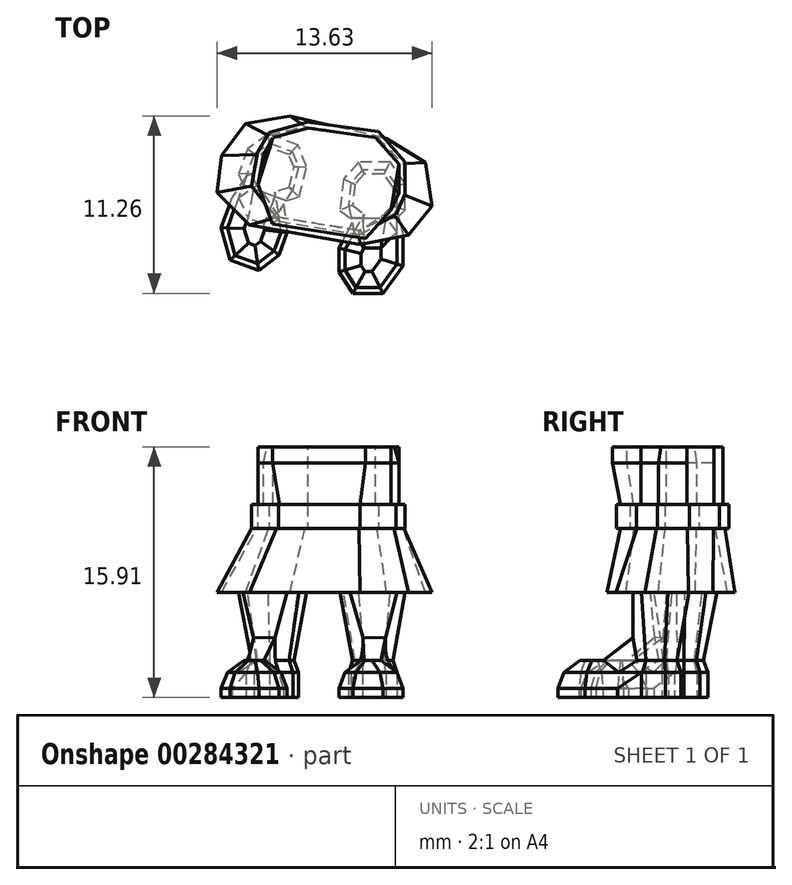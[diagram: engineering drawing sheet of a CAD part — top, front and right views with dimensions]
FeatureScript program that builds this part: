
annotation { "Feature Type Name" : "Feature", "Feature Type Description" : "" }
export const myFeature = defineFeature(function(context is Context, id is Id, definition is map)
    precondition{}
    {
        {
            var Q0;
            Q0=qCreatedBy(makeId("Top.planeOp"),FACE);
            var sketch = newSketch(context, id + "F0", { "sketchPlane" : qUnion([Q0])});
            skLineSegment(sketch, "E0.bottom", {"start": v(0, 0) * mm, "end": v(25.4, 0) * mm});
            skLineSegment(sketch, "E0.top", {"start": v(0, -25.4) * mm, "end": v(25.4, -25.4) * mm});
            skLineSegment(sketch, "E0.left", {"start": v(0, 0) * mm, "end": v(0, -25.4) * mm});
            skLineSegment(sketch, "E0.right", {"start": v(25.4, 0) * mm, "end": v(25.4, -25.4) * mm});
            skLineSegment(sketch, "E1", {"start": v(15.15, -16.75) * mm, "end": v(16.02, -18.11) * mm});
            skLineSegment(sketch, "E2", {"start": v(16.02, -18.11) * mm, "end": v(17.95, -18.11) * mm});
            skLineSegment(sketch, "E3", {"start": v(17.95, -18.11) * mm, "end": v(19.2, -16.37) * mm});
            skLineSegment(sketch, "E4", {"start": v(19.2, -16.37) * mm, "end": v(19.2, -14.33) * mm});
            skLineSegment(sketch, "E5", {"start": v(19.2, -14.33) * mm, "end": v(18.82, -12.78) * mm});
            skLineSegment(sketch, "E6", {"start": v(18.82, -12.78) * mm, "end": v(18.82, -11.27) * mm});
            skLineSegment(sketch, "E7", {"start": v(18.82, -11.27) * mm, "end": v(18.14, -10.28) * mm});
            skLineSegment(sketch, "E8", {"start": v(18.14, -10.28) * mm, "end": v(16.64, -10.28) * mm});
            skLineSegment(sketch, "E9", {"start": v(16.64, -10.28) * mm, "end": v(15.9, -11.08) * mm});
            skLineSegment(sketch, "E10", {"start": v(15.9, -11.08) * mm, "end": v(15.76, -12.51) * mm});
            skLineSegment(sketch, "E11", {"start": v(15.76, -12.51) * mm, "end": v(15.98, -13.61) * mm});
            skLineSegment(sketch, "E12", {"start": v(15.98, -13.61) * mm, "end": v(15.15, -15.24) * mm});
            skLineSegment(sketch, "E13", {"start": v(15.15, -15.24) * mm, "end": v(15.15, -16.75) * mm});
            skLineSegment(sketch, "E14.MirrorCS", {"start": v(11.34, -15.67) * mm, "end": v(10.05, -16.65) * mm});
            skLineSegment(sketch, "E15.MirrorCS", {"start": v(12.22, -11.48) * mm, "end": v(11.63, -12.43) * mm});
            skLineSegment(sketch, "E16.MirrorCS", {"start": v(12.15, -9.08) * mm, "end": v(12.56, -10.08) * mm});
            skLineSegment(sketch, "E17.MirrorCS", {"start": v(9.76, -9.26) * mm, "end": v(10.74, -8.57) * mm});
            skLineSegment(sketch, "E18.MirrorCS", {"start": v(8.24, -16) * mm, "end": v(7.66, -13.93) * mm});
            skLineSegment(sketch, "E19.MirrorCS", {"start": v(8.36, -12.01) * mm, "end": v(9.25, -10.68) * mm});
            skLineSegment(sketch, "E20.MirrorCS", {"start": v(10.74, -8.57) * mm, "end": v(12.15, -9.08) * mm});
            skLineSegment(sketch, "E21.MirrorCS", {"start": v(12.56, -10.08) * mm, "end": v(12.22, -11.48) * mm});
            skLineSegment(sketch, "E22.MirrorCS", {"start": v(11.63, -12.43) * mm, "end": v(11.85, -14.25) * mm});
            skLineSegment(sketch, "E23.MirrorCS", {"start": v(9.25, -10.68) * mm, "end": v(9.76, -9.26) * mm});
            skLineSegment(sketch, "E24.MirrorCS", {"start": v(11.85, -14.25) * mm, "end": v(11.34, -15.67) * mm});
            skLineSegment(sketch, "E25.MirrorCS", {"start": v(7.66, -13.93) * mm, "end": v(8.36, -12.01) * mm});
            skLineSegment(sketch, "E26.MirrorCS", {"start": v(10.05, -16.65) * mm, "end": v(8.24, -16) * mm});
            skSolve(sketch);
        }
        {
            var Q0;
            Q0=makeQuery(id+"F0.imprint","IMPRINT",FACE,{"disambiguationData":[TD([[makeQuery(id+"F0.imprint","IMPRINT",EDGE,{"derivedFrom":sQuery(id+"F0.wireOp",EDGE,"E0.bottom")}),-1.0]])]});
            cPlane(context, id + "F1", {"entities" : qUnion([Q0]), "cplaneType" : CPlaneType.OFFSET, "offset" : 1.59 * mm, "width" : 152.4 * mm, "height" : 152.4 * mm});
        }
        {
            var Q0;
            Q0=makeQuery(id+"F0.imprint","IMPRINT",FACE,{"disambiguationData":[TD([[makeQuery(id+"F0.imprint","IMPRINT",EDGE,{"derivedFrom":sQuery(id+"F0.wireOp",EDGE,"E14.MirrorCS")}),-1.0]])]});
            var Q1;
            Q1=makeQuery(id+"F0.imprint","IMPRINT",FACE,{"disambiguationData":[TD([[makeQuery(id+"F0.imprint","IMPRINT",EDGE,{"derivedFrom":sQuery(id+"F0.wireOp",EDGE,"E1")}),1.0]])]});
            extrude(context, id + "F2", {"entities" : qUnion([Q0, Q1]), "depth" : 1.59 * mm});
        }
        {
            var Q0;
            Q0=makeQuery(id+"F2.opExtrude","CAP_EDGE",EDGE,{"disambiguationData":[OSD([sQuery(id+"F0.wireOp",EDGE,"E4")])],"isStart":false});
            var Q1;
            Q1=makeQuery(id+"F2.opExtrude","CAP_EDGE",EDGE,{"disambiguationData":[OSD([sQuery(id+"F0.wireOp",EDGE,"E3")])],"isStart":false});
            var Q2;
            Q2=makeQuery(id+"F2.opExtrude","CAP_EDGE",EDGE,{"disambiguationData":[OSD([sQuery(id+"F0.wireOp",EDGE,"E2")])],"isStart":false});
            var Q3;
            Q3=makeQuery(id+"F2.opExtrude","CAP_EDGE",EDGE,{"disambiguationData":[OSD([sQuery(id+"F0.wireOp",EDGE,"E1")])],"isStart":false});
            var Q4;
            Q4=makeQuery(id+"F2.opExtrude","CAP_EDGE",EDGE,{"disambiguationData":[OSD([sQuery(id+"F0.wireOp",EDGE,"E13")])],"isStart":false});
            var Q5;
            Q5=makeQuery(id+"F2.opExtrude","CAP_EDGE",EDGE,{"disambiguationData":[OSD([sQuery(id+"F0.wireOp",EDGE,"E12")])],"isStart":false});
            chamfer(context, id + "F3", {"entities" : qUnion([Q0, Q1, Q2, Q3, Q4, Q5]), "chamferType" : ChamferType.TWO_OFFSETS, "width1" : 0.38 * mm, "oppositeDirection" : false, "width2" : 1.02 * mm, "tangentPropagation" : true});
        }
        {
            var Q0;
            Q0=makeQuery(id+"F2.opExtrude","CAP_EDGE",EDGE,{"disambiguationData":[OSD([sQuery(id+"F0.wireOp",EDGE,"E25.MirrorCS")])],"isStart":false});
            var Q1;
            Q1=makeQuery(id+"F2.opExtrude","CAP_EDGE",EDGE,{"disambiguationData":[OSD([sQuery(id+"F0.wireOp",EDGE,"E18.MirrorCS")])],"isStart":false});
            var Q2;
            Q2=makeQuery(id+"F2.opExtrude","CAP_EDGE",EDGE,{"disambiguationData":[OSD([sQuery(id+"F0.wireOp",EDGE,"E26.MirrorCS")])],"isStart":false});
            var Q3;
            Q3=makeQuery(id+"F2.opExtrude","CAP_EDGE",EDGE,{"disambiguationData":[OSD([sQuery(id+"F0.wireOp",EDGE,"E14.MirrorCS")])],"isStart":false});
            var Q4;
            Q4=makeQuery(id+"F2.opExtrude","CAP_EDGE",EDGE,{"disambiguationData":[OSD([sQuery(id+"F0.wireOp",EDGE,"E24.MirrorCS")])],"isStart":false});
            var Q5;
            Q5=makeQuery(id+"F2.opExtrude","CAP_EDGE",EDGE,{"disambiguationData":[OSD([sQuery(id+"F0.wireOp",EDGE,"E22.MirrorCS")])],"isStart":false});
            chamfer(context, id + "F4", {"entities" : qUnion([Q0, Q1, Q2, Q3, Q4, Q5]), "chamferType" : ChamferType.TWO_OFFSETS, "width1" : 1.02 * mm, "oppositeDirection" : false, "width2" : 0.38 * mm, "tangentPropagation" : true});
        }
        {
            var Q0;
            Q0=qCreatedBy(id+"F1.planeOp",FACE);
            var sketch = newSketch(context, id + "F5", { "sketchPlane" : qUnion([Q0])});
            skLineSegment(sketch, "E27.0.0", {"start": v(11.46, -14.2) * mm, "end": v(11.3, -12.95) * mm});
            skLineSegment(sketch, "E27.0.1", {"start": v(11.3, -12.95) * mm, "end": v(12.22, -11.48) * mm});
            skLineSegment(sketch, "E27.0.2", {"start": v(12.22, -11.48) * mm, "end": v(12.56, -10.08) * mm});
            skLineSegment(sketch, "E27.0.3", {"start": v(12.56, -10.08) * mm, "end": v(12.15, -9.08) * mm});
            skLineSegment(sketch, "E27.0.4", {"start": v(12.15, -9.08) * mm, "end": v(10.74, -8.57) * mm});
            skLineSegment(sketch, "E27.0.5", {"start": v(10.74, -8.57) * mm, "end": v(9.77, -9.26) * mm});
            skLineSegment(sketch, "E27.0.6", {"start": v(9.77, -9.26) * mm, "end": v(8.06, -13.94) * mm});
            skLineSegment(sketch, "E27.0.7", {"start": v(8.06, -13.94) * mm, "end": v(8.55, -15.7) * mm});
            skLineSegment(sketch, "E27.0.8", {"start": v(8.55, -15.7) * mm, "end": v(9.99, -16.22) * mm});
            skLineSegment(sketch, "E27.0.9", {"start": v(9.99, -16.22) * mm, "end": v(11.02, -15.43) * mm});
            skLineSegment(sketch, "E27.0.10", {"start": v(11.02, -15.43) * mm, "end": v(11.46, -14.2) * mm});
            skLineSegment(sketch, "E28.0.0", {"start": v(15.76, -12.51) * mm, "end": v(16.1, -14.2) * mm});
            skLineSegment(sketch, "E28.0.1", {"start": v(16.1, -14.2) * mm, "end": v(15.53, -15.33) * mm});
            skLineSegment(sketch, "E28.0.2", {"start": v(15.53, -15.33) * mm, "end": v(15.53, -16.64) * mm});
            skLineSegment(sketch, "E28.0.3", {"start": v(15.53, -16.64) * mm, "end": v(16.23, -17.73) * mm});
            skLineSegment(sketch, "E28.0.4", {"start": v(16.23, -17.73) * mm, "end": v(17.76, -17.73) * mm});
            skLineSegment(sketch, "E28.0.5", {"start": v(17.76, -17.73) * mm, "end": v(18.82, -16.25) * mm});
            skLineSegment(sketch, "E28.0.6", {"start": v(18.82, -16.25) * mm, "end": v(18.82, -11.26) * mm});
            skLineSegment(sketch, "E28.0.7", {"start": v(18.82, -11.26) * mm, "end": v(18.14, -10.28) * mm});
            skLineSegment(sketch, "E28.0.8", {"start": v(18.14, -10.28) * mm, "end": v(16.64, -10.28) * mm});
            skLineSegment(sketch, "E28.0.9", {"start": v(16.64, -10.28) * mm, "end": v(15.9, -11.08) * mm});
            skLineSegment(sketch, "E28.0.10", {"start": v(15.9, -11.08) * mm, "end": v(15.76, -12.51) * mm});
            skLineSegment(sketch, "E29", {"start": v(16.1, -14.2) * mm, "end": v(18.82, -14.2) * mm});
            skLineSegment(sketch, "E30", {"start": v(11.3, -12.95) * mm, "end": v(8.76, -12.03) * mm});
            skSolve(sketch);
        }
        {
            var Q0;
            Q0=qCreatedBy(id+"F1.planeOp",FACE);
            cPlane(context, id + "F6", {"entities" : qUnion([Q0]), "cplaneType" : CPlaneType.OFFSET, "offset" : 0.76 * mm, "width" : 152.4 * mm, "height" : 152.4 * mm});
        }
        {
            var Q0;
            Q0=qCreatedBy(id+"F6.planeOp",FACE);
            var sketch = newSketch(context, id + "F7", { "sketchPlane" : qUnion([Q0])});
            skLineSegment(sketch, "E31.0.0", {"start": v(8.76, -12.03) * mm, "end": v(11.3, -12.95) * mm, "construction": true});
            skLineSegment(sketch, "E31.0.1", {"start": v(11.3, -12.95) * mm, "end": v(12.22, -11.48) * mm, "construction": true});
            skLineSegment(sketch, "E31.0.2", {"start": v(12.22, -11.48) * mm, "end": v(12.56, -10.08) * mm, "construction": true});
            skLineSegment(sketch, "E31.0.3", {"start": v(12.56, -10.08) * mm, "end": v(12.15, -9.08) * mm, "construction": true});
            skLineSegment(sketch, "E31.0.4", {"start": v(12.15, -9.08) * mm, "end": v(10.74, -8.57) * mm, "construction": true});
            skLineSegment(sketch, "E31.0.5", {"start": v(10.74, -8.57) * mm, "end": v(9.77, -9.26) * mm, "construction": true});
            skLineSegment(sketch, "E31.0.6", {"start": v(9.77, -9.26) * mm, "end": v(8.76, -12.03) * mm, "construction": true});
            skLineSegment(sketch, "E32.0.0", {"start": v(11.3, -12.95) * mm, "end": v(8.76, -12.03) * mm, "construction": true});
            skLineSegment(sketch, "E32.0.1", {"start": v(8.76, -12.03) * mm, "end": v(8.06, -13.94) * mm, "construction": true});
            skLineSegment(sketch, "E32.0.2", {"start": v(8.06, -13.94) * mm, "end": v(8.55, -15.7) * mm, "construction": true});
            skLineSegment(sketch, "E32.0.3", {"start": v(8.55, -15.7) * mm, "end": v(9.99, -16.22) * mm, "construction": true});
            skLineSegment(sketch, "E32.0.4", {"start": v(9.99, -16.22) * mm, "end": v(11.02, -15.43) * mm, "construction": true});
            skLineSegment(sketch, "E32.0.5", {"start": v(11.02, -15.43) * mm, "end": v(11.46, -14.2) * mm, "construction": true});
            skLineSegment(sketch, "E32.0.6", {"start": v(11.46, -14.2) * mm, "end": v(11.3, -12.95) * mm, "construction": true});
            skLineSegment(sketch, "E33.0.0", {"start": v(16.1, -14.2) * mm, "end": v(18.82, -14.2) * mm, "construction": true});
            skLineSegment(sketch, "E33.0.1", {"start": v(18.82, -14.2) * mm, "end": v(18.82, -11.26) * mm, "construction": true});
            skLineSegment(sketch, "E33.0.2", {"start": v(18.82, -11.26) * mm, "end": v(18.14, -10.28) * mm, "construction": true});
            skLineSegment(sketch, "E33.0.3", {"start": v(18.14, -10.28) * mm, "end": v(16.64, -10.28) * mm, "construction": true});
            skLineSegment(sketch, "E33.0.4", {"start": v(16.64, -10.28) * mm, "end": v(15.9, -11.08) * mm, "construction": true});
            skLineSegment(sketch, "E33.0.5", {"start": v(15.9, -11.08) * mm, "end": v(15.76, -12.51) * mm, "construction": true});
            skLineSegment(sketch, "E33.0.6", {"start": v(15.76, -12.51) * mm, "end": v(16.1, -14.2) * mm, "construction": true});
            skLineSegment(sketch, "E34.0.0", {"start": v(18.82, -14.2) * mm, "end": v(16.1, -14.2) * mm, "construction": true});
            skLineSegment(sketch, "E34.0.1", {"start": v(16.1, -14.2) * mm, "end": v(15.53, -15.33) * mm, "construction": true});
            skLineSegment(sketch, "E34.0.2", {"start": v(15.53, -15.33) * mm, "end": v(15.53, -16.64) * mm, "construction": true});
            skLineSegment(sketch, "E34.0.3", {"start": v(15.53, -16.64) * mm, "end": v(16.23, -17.73) * mm, "construction": true});
            skLineSegment(sketch, "E34.0.4", {"start": v(16.23, -17.73) * mm, "end": v(17.76, -17.73) * mm, "construction": true});
            skLineSegment(sketch, "E34.0.5", {"start": v(17.76, -17.73) * mm, "end": v(18.82, -16.25) * mm, "construction": true});
            skLineSegment(sketch, "E34.0.6", {"start": v(18.82, -16.25) * mm, "end": v(18.82, -14.2) * mm, "construction": true});
            skLineSegment(sketch, "E35.0", {"start": v(10.42, -14.09) * mm, "end": v(10.38, -13.7) * mm});
            skLineSegment(sketch, "E35.1", {"start": v(10.16, -14.8) * mm, "end": v(10.42, -14.09) * mm});
            skLineSegment(sketch, "E35.2", {"start": v(9.37, -13.33) * mm, "end": v(9.13, -13.98) * mm});
            skLineSegment(sketch, "E35.3", {"start": v(9.13, -13.98) * mm, "end": v(9.4, -14.92) * mm});
            skLineSegment(sketch, "E35.4", {"start": v(9.4, -14.92) * mm, "end": v(9.81, -15.07) * mm});
            skLineSegment(sketch, "E35.5", {"start": v(10.38, -13.7) * mm, "end": v(9.37, -13.33) * mm});
            skLineSegment(sketch, "E35.6", {"start": v(9.81, -15.07) * mm, "end": v(10.16, -14.8) * mm});
            skLineSegment(sketch, "E36.0", {"start": v(9.98, -9.42) * mm, "end": v(9.09, -11.87) * mm, "construction": true});
            skLineSegment(sketch, "E36.1", {"start": v(10.78, -8.85) * mm, "end": v(9.98, -9.42) * mm});
            skLineSegment(sketch, "E36.2", {"start": v(11.2, -12.64) * mm, "end": v(11.98, -11.38) * mm, "construction": true});
            skLineSegment(sketch, "E36.3", {"start": v(11.98, -11.38) * mm, "end": v(12.3, -10.1) * mm});
            skLineSegment(sketch, "E36.4", {"start": v(12.3, -10.1) * mm, "end": v(11.96, -9.28) * mm});
            skLineSegment(sketch, "E36.5", {"start": v(9.09, -11.87) * mm, "end": v(11.2, -12.64) * mm, "construction": true});
            skLineSegment(sketch, "E36.6", {"start": v(11.96, -9.28) * mm, "end": v(10.78, -8.85) * mm});
            skLineSegment(sketch, "E37", {"start": v(11.98, -11.38) * mm, "end": v(11.1, -11.67) * mm});
            skLineSegment(sketch, "E38", {"start": v(11.1, -11.67) * mm, "end": v(9.9, -11.24) * mm});
            skLineSegment(sketch, "E39", {"start": v(9.9, -11.24) * mm, "end": v(9.58, -10.5) * mm});
            skLineSegment(sketch, "E40", {"start": v(9.58, -10.5) * mm, "end": v(11.98, -11.38) * mm, "construction": true});
            skLineSegment(sketch, "E41", {"start": v(11.96, -9.28) * mm, "end": v(11.1, -11.67) * mm, "construction": true});
            skLineSegment(sketch, "E42", {"start": v(9.9, -11.24) * mm, "end": v(10.78, -8.85) * mm, "construction": true});
            skLineSegment(sketch, "E43", {"start": v(9.98, -9.42) * mm, "end": v(9.58, -10.5) * mm});
            skLineSegment(sketch, "E44", {"start": v(9.37, -13.33) * mm, "end": v(9.9, -11.24) * mm});
            skLineSegment(sketch, "E45", {"start": v(11.1, -11.67) * mm, "end": v(10.38, -13.7) * mm});
            skLineSegment(sketch, "E46.0", {"start": v(16.73, -15.22) * mm, "end": v(16.55, -15.57) * mm});
            skLineSegment(sketch, "E46.1", {"start": v(16.55, -15.57) * mm, "end": v(16.55, -16.34) * mm});
            skLineSegment(sketch, "E46.2", {"start": v(17.8, -15.92) * mm, "end": v(17.8, -15.22) * mm});
            skLineSegment(sketch, "E46.3", {"start": v(17.23, -16.71) * mm, "end": v(17.8, -15.92) * mm});
            skLineSegment(sketch, "E46.4", {"start": v(16.79, -16.71) * mm, "end": v(17.23, -16.71) * mm});
            skLineSegment(sketch, "E46.5", {"start": v(16.73, -15.22) * mm, "end": v(17.8, -15.22) * mm});
            skLineSegment(sketch, "E46.6", {"start": v(16.55, -16.34) * mm, "end": v(16.79, -16.71) * mm});
            skLineSegment(sketch, "E47.0", {"start": v(16.31, -13.95) * mm, "end": v(18.56, -13.95) * mm, "construction": true});
            skLineSegment(sketch, "E47.1", {"start": v(16.01, -12.5) * mm, "end": v(16.31, -13.95) * mm, "construction": true});
            skLineSegment(sketch, "E47.2", {"start": v(18.56, -11.34) * mm, "end": v(18, -10.54) * mm});
            skLineSegment(sketch, "E47.3", {"start": v(18, -10.54) * mm, "end": v(16.75, -10.54) * mm});
            skLineSegment(sketch, "E47.4", {"start": v(16.75, -10.54) * mm, "end": v(16.15, -11.19) * mm});
            skLineSegment(sketch, "E47.5", {"start": v(18.56, -13.95) * mm, "end": v(18.56, -11.34) * mm, "construction": true});
            skLineSegment(sketch, "E47.6", {"start": v(16.15, -11.19) * mm, "end": v(16.01, -12.5) * mm});
            skLineSegment(sketch, "E48", {"start": v(16.01, -12.5) * mm, "end": v(18.56, -12.5) * mm, "construction": true});
            skLineSegment(sketch, "E49", {"start": v(18.56, -12.5) * mm, "end": v(18, -13.08) * mm});
            skLineSegment(sketch, "E50", {"start": v(18, -13.08) * mm, "end": v(17.8, -15.22) * mm});
            skLineSegment(sketch, "E51", {"start": v(16.01, -12.5) * mm, "end": v(16.75, -13.08) * mm});
            skLineSegment(sketch, "E52", {"start": v(16.75, -13.08) * mm, "end": v(16.73, -15.22) * mm});
            skLineSegment(sketch, "E53", {"start": v(16.75, -10.54) * mm, "end": v(16.75, -13.08) * mm, "construction": true});
            skLineSegment(sketch, "E54", {"start": v(18, -13.08) * mm, "end": v(16.75, -13.08) * mm});
            skLineSegment(sketch, "E55", {"start": v(18, -13.08) * mm, "end": v(18, -10.54) * mm, "construction": true});
            skLineSegment(sketch, "E56", {"start": v(18.56, -11.34) * mm, "end": v(18.56, -12.5) * mm});
            skSolve(sketch);
        }
        {
            var Q1;
            Q1=makeQuery(id+"F5.imprint","IMPRINT",FACE,{"disambiguationData":[TD([[makeQuery(id+"F5.imprint","IMPRINT",EDGE,{"derivedFrom":sQuery(id+"F5.wireOp",EDGE,"E27.0.1")}),1.0]])]});
            var Q2;
            Q2=makeQuery(id+"F7.imprint","IMPRINT",FACE,{"disambiguationData":[TD([[makeQuery(id+"F7.imprint","IMPRINT",EDGE,{"derivedFrom":sQuery(id+"F7.wireOp",EDGE,"E36.1")}),1.0]])]});
            var Q3;
            Q3=sQuery(id+"F5.wireOp",VERTEX,"E27.0.6.start");
            var Q4;
            Q4=sQuery(id+"F7.wireOp",VERTEX,"E36.1.end");
            loft(context, id + "F8", {"operationType" : NewBodyOperationType.ADD, "sheetProfilesArray" : [{ "sheetProfileEntities" : qUnion([Q1]) }, { "sheetProfileEntities" : qUnion([Q2]) }], "matchConnections" : true, "connections" : [{ "connectionEntities" : qUnion([Q3, Q4]), "connectionEdgeQueries" : qUnion([]), "connectionEdgeParameters" : [] }]});
        }
        {
            var Q1;
            Q1=makeQuery(id+"F5.imprint","IMPRINT",FACE,{"disambiguationData":[TD([[makeQuery(id+"F5.imprint","IMPRINT",EDGE,{"derivedFrom":sQuery(id+"F5.wireOp",EDGE,"E28.0.0")}),1.0]])]});
            var Q2;
            Q2=makeQuery(id+"F7.imprint","IMPRINT",FACE,{"disambiguationData":[TD([[makeQuery(id+"F7.imprint","IMPRINT",EDGE,{"derivedFrom":sQuery(id+"F7.wireOp",EDGE,"E47.2")}),1.0]])]});
            var Q3;
            Q3=sQuery(id+"F5.wireOp",VERTEX,"E29.end");
            var Q4;
            Q4=sQuery(id+"F7.wireOp",VERTEX,"E50.start");
            loft(context, id + "F9", {"operationType" : NewBodyOperationType.ADD, "sheetProfilesArray" : [{ "sheetProfileEntities" : qUnion([Q1]) }, { "sheetProfileEntities" : qUnion([Q2]) }], "matchConnections" : true, "connections" : [{ "connectionEntities" : qUnion([Q3, Q4]), "connectionEdgeQueries" : qUnion([]), "connectionEdgeParameters" : [] }]});
        }
        {
            var Q1;
            Q1=makeQuery(id+"F5.imprint","IMPRINT",FACE,{"disambiguationData":[TD([[makeQuery(id+"F5.imprint","IMPRINT",EDGE,{"derivedFrom":sQuery(id+"F5.wireOp",EDGE,"E27.0.0")}),1.0]])]});
            var Q2;
            Q2=makeQuery(id+"F7.imprint","IMPRINT",FACE,{"disambiguationData":[TD([[makeQuery(id+"F7.imprint","IMPRINT",EDGE,{"derivedFrom":sQuery(id+"F7.wireOp",EDGE,"E35.0")}),1.0]])]});
            loft(context, id + "F10", {"operationType" : NewBodyOperationType.ADD, "sheetProfilesArray" : [{ "sheetProfileEntities" : qUnion([Q1]) }, { "sheetProfileEntities" : qUnion([Q2]) }]});
        }
        {
            var Q1;
            Q1=makeQuery(id+"F5.imprint","IMPRINT",FACE,{"disambiguationData":[TD([[makeQuery(id+"F5.imprint","IMPRINT",EDGE,{"derivedFrom":sQuery(id+"F5.wireOp",EDGE,"E28.0.1")}),1.0]])]});
            var Q2;
            Q2=makeQuery(id+"F7.imprint","IMPRINT",FACE,{"disambiguationData":[TD([[makeQuery(id+"F7.imprint","IMPRINT",EDGE,{"derivedFrom":sQuery(id+"F7.wireOp",EDGE,"E46.0")}),1.0]])]});
            loft(context, id + "F11", {"operationType" : NewBodyOperationType.ADD, "sheetProfilesArray" : [{ "sheetProfileEntities" : qUnion([Q1]) }, { "sheetProfileEntities" : qUnion([Q2]) }]});
        }
        {
            var Q0;
            Q0=qCreatedBy(id+"F6.planeOp",FACE);
            cPlane(context, id + "F12", {"entities" : qUnion([Q0]), "cplaneType" : CPlaneType.OFFSET, "offset" : 4.32 * mm, "width" : 152.4 * mm, "height" : 152.4 * mm});
        }
        {
            var Q0;
            Q0=qCreatedBy(id+"F12.planeOp",FACE);
            var sketch = newSketch(context, id + "F13", { "sketchPlane" : qUnion([Q0])});
            skLineSegment(sketch, "E57.0.0", {"start": v(11.1, -11.67) * mm, "end": v(11.98, -11.38) * mm, "construction": true});
            skLineSegment(sketch, "E57.0.1", {"start": v(11.98, -11.38) * mm, "end": v(12.3, -10.1) * mm, "construction": true});
            skLineSegment(sketch, "E57.0.2", {"start": v(12.3, -10.1) * mm, "end": v(11.96, -9.28) * mm, "construction": true});
            skLineSegment(sketch, "E57.0.3", {"start": v(11.96, -9.28) * mm, "end": v(10.78, -8.85) * mm, "construction": true});
            skLineSegment(sketch, "E57.0.4", {"start": v(10.78, -8.85) * mm, "end": v(9.98, -9.42) * mm, "construction": true});
            skLineSegment(sketch, "E57.0.5", {"start": v(9.98, -9.42) * mm, "end": v(9.58, -10.5) * mm, "construction": true});
            skLineSegment(sketch, "E57.0.6", {"start": v(9.58, -10.5) * mm, "end": v(9.9, -11.24) * mm, "construction": true});
            skLineSegment(sketch, "E57.0.7", {"start": v(9.9, -11.24) * mm, "end": v(11.1, -11.67) * mm, "construction": true});
            skLineSegment(sketch, "E58.0.0", {"start": v(18, -13.08) * mm, "end": v(18.56, -12.5) * mm, "construction": true});
            skLineSegment(sketch, "E58.0.1", {"start": v(18.56, -12.5) * mm, "end": v(18.56, -11.34) * mm, "construction": true});
            skLineSegment(sketch, "E58.0.2", {"start": v(18.56, -11.34) * mm, "end": v(18, -10.54) * mm, "construction": true});
            skLineSegment(sketch, "E58.0.3", {"start": v(18, -10.54) * mm, "end": v(16.75, -10.54) * mm, "construction": true});
            skLineSegment(sketch, "E58.0.4", {"start": v(16.75, -10.54) * mm, "end": v(16.15, -11.19) * mm, "construction": true});
            skLineSegment(sketch, "E58.0.5", {"start": v(16.15, -11.19) * mm, "end": v(16.01, -12.5) * mm, "construction": true});
            skLineSegment(sketch, "E58.0.6", {"start": v(16.01, -12.5) * mm, "end": v(16.75, -13.08) * mm, "construction": true});
            skLineSegment(sketch, "E58.0.7", {"start": v(16.75, -13.08) * mm, "end": v(18, -13.08) * mm, "construction": true});
            skLineSegment(sketch, "E59.0", {"start": v(19.33, -12.8) * mm, "end": v(19.33, -11.1) * mm});
            skLineSegment(sketch, "E59.1", {"start": v(18.33, -13.84) * mm, "end": v(19.33, -12.8) * mm});
            skLineSegment(sketch, "E59.2", {"start": v(19.33, -11.1) * mm, "end": v(18.4, -9.78) * mm});
            skLineSegment(sketch, "E59.3", {"start": v(16.49, -13.84) * mm, "end": v(18.33, -13.84) * mm});
            skLineSegment(sketch, "E59.4", {"start": v(18.4, -9.78) * mm, "end": v(16.41, -9.78) * mm});
            skLineSegment(sketch, "E59.5", {"start": v(16.41, -9.78) * mm, "end": v(15.42, -10.86) * mm});
            skLineSegment(sketch, "E59.6", {"start": v(15.42, -10.86) * mm, "end": v(15.21, -12.84) * mm});
            skLineSegment(sketch, "E59.7", {"start": v(15.21, -12.84) * mm, "end": v(16.49, -13.84) * mm});
            skLineSegment(sketch, "E60.0", {"start": v(10.66, -8) * mm, "end": v(9.35, -8.94) * mm});
            skLineSegment(sketch, "E60.1", {"start": v(12.54, -8.68) * mm, "end": v(10.66, -8) * mm});
            skLineSegment(sketch, "E60.2", {"start": v(9.35, -8.94) * mm, "end": v(8.76, -10.54) * mm});
            skLineSegment(sketch, "E60.3", {"start": v(13.1, -10.04) * mm, "end": v(12.54, -8.68) * mm});
            skLineSegment(sketch, "E60.4", {"start": v(8.76, -10.54) * mm, "end": v(9.34, -11.85) * mm});
            skLineSegment(sketch, "E60.5", {"start": v(9.34, -11.85) * mm, "end": v(11.08, -12.48) * mm});
            skLineSegment(sketch, "E60.6", {"start": v(11.08, -12.48) * mm, "end": v(12.62, -11.97) * mm});
            skLineSegment(sketch, "E60.7", {"start": v(12.62, -11.97) * mm, "end": v(13.1, -10.04) * mm});
            skSolve(sketch);
        }
        {
            var Q1;
            Q1=makeQuery(id+"F8.opLoft","CAP_FACE",FACE,{"disambiguationData":[OSD([makeQuery(id+"F7.imprint","IMPRINT",FACE,{"disambiguationData":[TD([[makeQuery(id+"F7.imprint","IMPRINT",EDGE,{"derivedFrom":sQuery(id+"F7.wireOp",EDGE,"E36.1")}),1.0]])]})])],"isStart":true});
            var Q2;
            Q2=makeQuery(id+"F13.imprint","IMPRINT",FACE,{"disambiguationData":[TD([[makeQuery(id+"F13.imprint","IMPRINT",EDGE,{"derivedFrom":sQuery(id+"F13.wireOp",EDGE,"E60.0")}),1.0]])]});
            loft(context, id + "F14", {"operationType" : NewBodyOperationType.ADD, "sheetProfilesArray" : [{ "sheetProfileEntities" : qUnion([Q1]) }, { "sheetProfileEntities" : qUnion([Q2]) }]});
        }
        {
            var Q1;
            Q1=makeQuery(id+"F9.opLoft","CAP_FACE",FACE,{"disambiguationData":[OSD([makeQuery(id+"F7.imprint","IMPRINT",FACE,{"disambiguationData":[TD([[makeQuery(id+"F7.imprint","IMPRINT",EDGE,{"derivedFrom":sQuery(id+"F7.wireOp",EDGE,"E47.2")}),1.0]])]})])],"isStart":true});
            var Q2;
            Q2=makeQuery(id+"F13.imprint","IMPRINT",FACE,{"disambiguationData":[TD([[makeQuery(id+"F13.imprint","IMPRINT",EDGE,{"derivedFrom":sQuery(id+"F13.wireOp",EDGE,"E59.0")}),1.0]])]});
            loft(context, id + "F15", {"operationType" : NewBodyOperationType.ADD, "sheetProfilesArray" : [{ "sheetProfileEntities" : qUnion([Q1]) }, { "sheetProfileEntities" : qUnion([Q2]) }]});
        }
        {
            var Q0;
            Q0=makeQuery(id+"F15.opLoft","CAP_FACE",FACE,{"disambiguationData":[OSD([makeQuery(id+"F13.imprint","IMPRINT",FACE,{"disambiguationData":[TD([[makeQuery(id+"F13.imprint","IMPRINT",EDGE,{"derivedFrom":sQuery(id+"F13.wireOp",EDGE,"E59.0")}),1.0]])]})])],"isStart":true});
            var sketch = newSketch(context, id + "F16", { "sketchPlane" : qUnion([Q0])});
            skLineSegment(sketch, "E61.0.0", {"start": v(15.42, -10.86) * mm, "end": v(15.21, -12.84) * mm});
            skLineSegment(sketch, "E61.0.1", {"start": v(15.21, -12.84) * mm, "end": v(16.49, -13.84) * mm});
            skLineSegment(sketch, "E61.0.2", {"start": v(16.49, -13.84) * mm, "end": v(18.33, -13.84) * mm});
            skLineSegment(sketch, "E61.0.3", {"start": v(18.33, -13.84) * mm, "end": v(19.33, -12.8) * mm});
            skLineSegment(sketch, "E61.0.4", {"start": v(19.33, -12.8) * mm, "end": v(19.33, -11.1) * mm});
            skLineSegment(sketch, "E61.0.5", {"start": v(19.33, -11.1) * mm, "end": v(18.4, -9.78) * mm});
            skLineSegment(sketch, "E61.0.6", {"start": v(18.4, -9.78) * mm, "end": v(16.41, -9.78) * mm});
            skLineSegment(sketch, "E61.0.7", {"start": v(16.41, -9.78) * mm, "end": v(15.42, -10.86) * mm});
            skLineSegment(sketch, "E62.0.0", {"start": v(11.08, -12.48) * mm, "end": v(12.62, -11.97) * mm});
            skLineSegment(sketch, "E62.0.1", {"start": v(12.62, -11.97) * mm, "end": v(13.1, -10.04) * mm});
            skLineSegment(sketch, "E62.0.2", {"start": v(13.1, -10.04) * mm, "end": v(12.54, -8.68) * mm});
            skLineSegment(sketch, "E62.0.3", {"start": v(12.54, -8.68) * mm, "end": v(10.66, -8) * mm});
            skLineSegment(sketch, "E62.0.4", {"start": v(10.66, -8) * mm, "end": v(9.35, -8.94) * mm});
            skLineSegment(sketch, "E62.0.5", {"start": v(9.35, -8.94) * mm, "end": v(8.76, -10.54) * mm});
            skLineSegment(sketch, "E62.0.6", {"start": v(8.76, -10.54) * mm, "end": v(9.34, -11.85) * mm});
            skLineSegment(sketch, "E62.0.7", {"start": v(9.34, -11.85) * mm, "end": v(11.08, -12.48) * mm});
            skLineSegment(sketch, "E63", {"start": v(15.85, -13.34) * mm, "end": v(18.83, -13.32) * mm});
            skLineSegment(sketch, "E64", {"start": v(9.05, -11.2) * mm, "end": v(11.85, -12.23) * mm});
            skSolve(sketch);
        }
        {
            var Q0;
            {var subQ0=sQuery(id+"F16.wireOp",EDGE,"E61.0.2");Q0=makeQuery(id+"F16.imprint","IMPRINT",FACE,{"disambiguationData":[TD([[makeQuery(id+"F16.imprint","IMPRINT",EDGE,{"derivedFrom":subQ0}),1.0]])]});}
            var Q1;
            {var subQ0=sQuery(id+"F16.wireOp",EDGE,"E62.0.7");Q1=makeQuery(id+"F16.imprint","IMPRINT",FACE,{"disambiguationData":[TD([[makeQuery(id+"F16.imprint","IMPRINT",EDGE,{"derivedFrom":subQ0}),1.0]])]});}
            extrude(context, id + "F17", {"entities" : qUnion([Q0, Q1]), "operationType" : NewBodyOperationType.REMOVE, "oppositeDirection" : true, "depth" : 3.8 * mm});
        }
        {
            var Q1;
            Q1=makeQuery(id+"F15.opLoft","SWEPT_FACE",FACE,{"disambiguationData":[OSD([sQuery(id+"F7.wireOp",EDGE,"E49"),sQuery(id+"F7.wireOp",EDGE,"E50"),sQuery(id+"F7.wireOp",EDGE,"E51"),sQuery(id+"F7.wireOp",EDGE,"E52"),sQuery(id+"F7.wireOp",EDGE,"E54"),sQuery(id+"F13.wireOp",EDGE,"E59.1"),sQuery(id+"F13.wireOp",EDGE,"E59.3"),sQuery(id+"F13.wireOp",EDGE,"E59.7")])]});
            var Q2;
            Q2=makeQuery(id+"F11.opLoft","SWEPT_FACE",FACE,{"disambiguationData":[OSD([sQuery(id+"F5.wireOp",EDGE,"E28.0.0"),sQuery(id+"F5.wireOp",EDGE,"E28.0.1"),sQuery(id+"F5.wireOp",EDGE,"E28.0.6"),sQuery(id+"F5.wireOp",EDGE,"E29"),sQuery(id+"F7.wireOp",EDGE,"E46.0"),sQuery(id+"F7.wireOp",EDGE,"E46.2"),sQuery(id+"F7.wireOp",EDGE,"E46.5"),sQuery(id+"F7.wireOp",EDGE,"E50"),sQuery(id+"F7.wireOp",EDGE,"E52")])]});
            loft(context, id + "F18", {"operationType" : NewBodyOperationType.ADD, "sheetProfilesArray" : [{ "sheetProfileEntities" : qUnion([Q1]) }, { "sheetProfileEntities" : qUnion([Q2]) }]});
        }
        {
            var Q1;
            Q1=makeQuery(id+"F14.opLoft","SWEPT_FACE",FACE,{"disambiguationData":[OSD([sQuery(id+"F7.wireOp",EDGE,"E37"),sQuery(id+"F7.wireOp",EDGE,"E38"),sQuery(id+"F7.wireOp",EDGE,"E39"),sQuery(id+"F7.wireOp",EDGE,"E44"),sQuery(id+"F7.wireOp",EDGE,"E45"),sQuery(id+"F13.wireOp",EDGE,"E60.4"),sQuery(id+"F13.wireOp",EDGE,"E60.5"),sQuery(id+"F13.wireOp",EDGE,"E60.6")])]});
            var Q2;
            Q2=makeQuery(id+"F10.opLoft","SWEPT_FACE",FACE,{"disambiguationData":[OSD([sQuery(id+"F5.wireOp",EDGE,"E27.0.0"),sQuery(id+"F5.wireOp",EDGE,"E27.0.1"),sQuery(id+"F5.wireOp",EDGE,"E27.0.6"),sQuery(id+"F5.wireOp",EDGE,"E30"),sQuery(id+"F7.wireOp",EDGE,"E35.0"),sQuery(id+"F7.wireOp",EDGE,"E35.2"),sQuery(id+"F7.wireOp",EDGE,"E35.5"),sQuery(id+"F7.wireOp",EDGE,"E44"),sQuery(id+"F7.wireOp",EDGE,"E45")])]});
            loft(context, id + "F19", {"operationType" : NewBodyOperationType.ADD, "sheetProfilesArray" : [{ "sheetProfileEntities" : qUnion([Q1]) }, { "sheetProfileEntities" : qUnion([Q2]) }]});
        }
        {
            var Q0;
            Q0=qCreatedBy(id+"F12.planeOp",FACE);
            var sketch = newSketch(context, id + "F20", { "sketchPlane" : qUnion([Q0])});
            skLineSegment(sketch, "E65", {"start": v(7.68, -9.37) * mm, "end": v(7.4, -11.71) * mm});
            skLineSegment(sketch, "E66", {"start": v(7.4, -11.71) * mm, "end": v(9.47, -13.77) * mm});
            skLineSegment(sketch, "E67", {"start": v(9.47, -13.77) * mm, "end": v(16.47, -15) * mm});
            skLineSegment(sketch, "E68", {"start": v(16.47, -15) * mm, "end": v(19.56, -14.42) * mm});
            skLineSegment(sketch, "E69", {"start": v(19.56, -14.42) * mm, "end": v(21.04, -12.57) * mm});
            skLineSegment(sketch, "E70", {"start": v(21.04, -12.57) * mm, "end": v(20.65, -9.8) * mm});
            skLineSegment(sketch, "E71", {"start": v(20.65, -9.8) * mm, "end": v(18.18, -8.26) * mm});
            skLineSegment(sketch, "E72", {"start": v(18.18, -8.26) * mm, "end": v(12.04, -6.85) * mm});
            skLineSegment(sketch, "E73", {"start": v(12.04, -6.85) * mm, "end": v(9.22, -7.32) * mm});
            skLineSegment(sketch, "E74", {"start": v(9.22, -7.32) * mm, "end": v(7.68, -9.37) * mm});
            skSolve(sketch);
        }
        {
            var Q0;
            Q0=qCreatedBy(id+"F12.planeOp",FACE);
            cPlane(context, id + "F21", {"entities" : qUnion([Q0]), "cplaneType" : CPlaneType.OFFSET, "offset" : 4.83 * mm, "width" : 152.4 * mm, "height" : 152.4 * mm});
        }
        {
            var Q0;
            Q0=qCreatedBy(id+"F21.planeOp",FACE);
            var sketch = newSketch(context, id + "F22", { "sketchPlane" : qUnion([Q0])});
            skLineSegment(sketch, "E75", {"start": v(19.28, 6.58) * mm, "end": v(19.28, -12.05) * mm, "construction": true});
            skLineSegment(sketch, "E76", {"start": v(10.34, 2.97) * mm, "end": v(10.34, -15.66) * mm, "construction": true});
            skLineSegment(sketch, "E77", {"start": v(18.46, -12.83) * mm, "end": v(18.96, -11.7) * mm});
            skLineSegment(sketch, "E78", {"start": v(18.96, -11.7) * mm, "end": v(18.96, -9.9) * mm});
            skLineSegment(sketch, "E79", {"start": v(18.96, -9.9) * mm, "end": v(17.46, -8.2) * mm});
            skLineSegment(sketch, "E80", {"start": v(17.46, -8.2) * mm, "end": v(13.17, -7.62) * mm});
            skLineSegment(sketch, "E81", {"start": v(13.17, -7.62) * mm, "end": v(10.95, -8.22) * mm});
            skLineSegment(sketch, "E82", {"start": v(10.95, -8.22) * mm, "end": v(10.34, -9.28) * mm});
            skLineSegment(sketch, "E83", {"start": v(10.34, -9.28) * mm, "end": v(10, -11.2) * mm});
            skLineSegment(sketch, "E84", {"start": v(10, -11.2) * mm, "end": v(11.52, -13.17) * mm});
            skLineSegment(sketch, "E85", {"start": v(11.52, -13.17) * mm, "end": v(16.4, -13.98) * mm});
            skLineSegment(sketch, "E86", {"start": v(16.4, -13.98) * mm, "end": v(18.46, -12.83) * mm});
            skLineSegment(sketch, "E87.0", {"start": v(19.34, -9.75) * mm, "end": v(17.65, -7.84) * mm});
            skLineSegment(sketch, "E87.1", {"start": v(19.34, -11.78) * mm, "end": v(19.34, -9.75) * mm});
            skLineSegment(sketch, "E87.2", {"start": v(17.65, -7.84) * mm, "end": v(13.14, -7.23) * mm});
            skLineSegment(sketch, "E87.3", {"start": v(18.75, -13.1) * mm, "end": v(19.34, -11.78) * mm});
            skLineSegment(sketch, "E87.4", {"start": v(16.47, -14.37) * mm, "end": v(18.75, -13.1) * mm});
            skLineSegment(sketch, "E87.5", {"start": v(11.3, -13.53) * mm, "end": v(16.47, -14.37) * mm});
            skLineSegment(sketch, "E87.6", {"start": v(13.14, -7.23) * mm, "end": v(10.7, -7.9) * mm});
            skLineSegment(sketch, "E87.7", {"start": v(10.7, -7.9) * mm, "end": v(9.98, -9.15) * mm});
            skLineSegment(sketch, "E87.8", {"start": v(9.98, -9.15) * mm, "end": v(9.6, -11.3) * mm});
            skLineSegment(sketch, "E87.9", {"start": v(9.6, -11.3) * mm, "end": v(11.3, -13.53) * mm});
            skSolve(sketch);
        }
        {
            var Q0;
            Q0=makeQuery(id+"F20.imprint","IMPRINT",FACE,{"disambiguationData":[TD([[makeQuery(id+"F20.imprint","IMPRINT",EDGE,{"derivedFrom":sQuery(id+"F20.wireOp",EDGE,"E65")}),1.0]])]});
            var Q1;
            Q1=makeQuery(id+"F22.imprint","IMPRINT",FACE,{"disambiguationData":[TD([[makeQuery(id+"F22.imprint","IMPRINT",EDGE,{"derivedFrom":sQuery(id+"F22.wireOp",EDGE,"E77")}),1.0]])]});
            loft(context, id + "F23", {"sheetProfilesArray" : [{ "sheetProfileEntities" : qUnion([Q0]) }, { "sheetProfileEntities" : qUnion([Q1]) }]});
        }
        {
            var Q0;
            Q0=qCreatedBy(id+"F21.planeOp",FACE);
            cPlane(context, id + "F24", {"entities" : qUnion([Q0]), "cplaneType" : CPlaneType.OFFSET, "offset" : 3.4 * mm, "width" : 152.4 * mm, "height" : 152.4 * mm});
        }
        {
            var Q0;
            Q0=qCreatedBy(id+"F24.planeOp",FACE);
            var sketch = newSketch(context, id + "F25", { "sketchPlane" : qUnion([Q0])});
            skLineSegment(sketch, "E88.0.0", {"start": v(11.52, -13.17) * mm, "end": v(16.4, -13.98) * mm, "construction": true});
            skLineSegment(sketch, "E88.0.1", {"start": v(16.4, -13.98) * mm, "end": v(18.46, -12.83) * mm, "construction": true});
            skLineSegment(sketch, "E88.0.2", {"start": v(18.46, -12.83) * mm, "end": v(18.96, -11.7) * mm});
            skLineSegment(sketch, "E88.0.3", {"start": v(18.96, -11.7) * mm, "end": v(18.96, -9.9) * mm});
            skLineSegment(sketch, "E88.0.4", {"start": v(18.96, -9.9) * mm, "end": v(17.46, -8.2) * mm});
            skLineSegment(sketch, "E88.0.5", {"start": v(17.46, -8.2) * mm, "end": v(13.17, -7.62) * mm});
            skLineSegment(sketch, "E88.0.6", {"start": v(13.17, -7.62) * mm, "end": v(10.95, -8.22) * mm});
            skLineSegment(sketch, "E88.0.7", {"start": v(10.95, -8.22) * mm, "end": v(10.34, -9.28) * mm});
            skLineSegment(sketch, "E88.0.8", {"start": v(10.34, -9.28) * mm, "end": v(10, -11.2) * mm});
            skLineSegment(sketch, "E88.0.9", {"start": v(10, -11.2) * mm, "end": v(11.52, -13.17) * mm, "construction": true});
            skLineSegment(sketch, "E89", {"start": v(10, -11.2) * mm, "end": v(10.92, -13.7) * mm});
            skLineSegment(sketch, "E90", {"start": v(10.92, -13.7) * mm, "end": v(16.83, -14.64) * mm});
            skLineSegment(sketch, "E91", {"start": v(16.83, -14.64) * mm, "end": v(18.46, -12.83) * mm});
            skSolve(sketch);
        }
        {
            var Q1;
            Q1=makeQuery(id+"F23.opLoft","CAP_FACE",FACE,{"disambiguationData":[OSD([makeQuery(id+"F22.imprint","IMPRINT",FACE,{"disambiguationData":[TD([[makeQuery(id+"F22.imprint","IMPRINT",EDGE,{"derivedFrom":sQuery(id+"F22.wireOp",EDGE,"E77")}),1.0]])]})])],"isStart":true});
            var Q2;
            Q2=makeQuery(id+"F25.imprint","IMPRINT",FACE,{"disambiguationData":[TD([[makeQuery(id+"F25.imprint","IMPRINT",EDGE,{"derivedFrom":sQuery(id+"F25.wireOp",EDGE,"E88.0.2")}),1.0]])]});
            loft(context, id + "F26", {"operationType" : NewBodyOperationType.ADD, "sheetProfilesArray" : [{ "sheetProfileEntities" : qUnion([Q1]) }, { "sheetProfileEntities" : qUnion([Q2]) }]});
        }
        {
            var Q0;
            Q0=makeQuery(id+"F22.imprint","IMPRINT",FACE,{"disambiguationData":[TD([[makeQuery(id+"F22.imprint","IMPRINT",EDGE,{"derivedFrom":sQuery(id+"F22.wireOp",EDGE,"E77")}),-1.0]])]});
            extrude(context, id + "F27", {"entities" : qUnion([Q0]), "operationType" : NewBodyOperationType.ADD, "endBound" : BoundingType.SYMMETRIC, "depth" : 1.52 * mm});
        }
        {
            var Q0;
            Q0=qCreatedBy(id+"F24.planeOp",FACE);
            cPlane(context, id + "F28", {"entities" : qUnion([Q0]), "cplaneType" : CPlaneType.OFFSET, "offset" : 1.02 * mm, "width" : 152.4 * mm, "height" : 152.4 * mm});
        }
        {
            var Q0;
            Q0=qCreatedBy(id+"F28.planeOp",FACE);
            var sketch = newSketch(context, id + "F29", { "sketchPlane" : qUnion([Q0])});
            skLineSegment(sketch, "E92.0.0", {"start": v(10.92, -13.7) * mm, "end": v(16.83, -14.64) * mm});
            skLineSegment(sketch, "E92.0.1", {"start": v(16.83, -14.64) * mm, "end": v(18.46, -12.83) * mm});
            skLineSegment(sketch, "E92.0.2", {"start": v(18.46, -12.83) * mm, "end": v(18.96, -11.7) * mm, "construction": true});
            skLineSegment(sketch, "E92.0.3", {"start": v(18.96, -11.7) * mm, "end": v(18.96, -9.9) * mm, "construction": true});
            skLineSegment(sketch, "E92.0.4", {"start": v(18.96, -9.9) * mm, "end": v(17.46, -8.2) * mm});
            skLineSegment(sketch, "E92.0.5", {"start": v(17.46, -8.2) * mm, "end": v(13.17, -7.62) * mm});
            skLineSegment(sketch, "E92.0.6", {"start": v(13.17, -7.62) * mm, "end": v(10.95, -8.22) * mm});
            skLineSegment(sketch, "E92.0.7", {"start": v(10.95, -8.22) * mm, "end": v(10.34, -9.28) * mm, "construction": true});
            skLineSegment(sketch, "E92.0.8", {"start": v(10.34, -9.28) * mm, "end": v(10, -11.2) * mm, "construction": true});
            skLineSegment(sketch, "E92.0.9", {"start": v(10, -11.2) * mm, "end": v(10.92, -13.7) * mm});
            skPoint(sketch, "E93", {"position": v(10.57, -9.4) * mm});
            skPoint(sketch, "E94", {"position": v(18.68, -11.54) * mm});
            skLineSegment(sketch, "E95", {"start": v(10.95, -8.22) * mm, "end": v(10.57, -9.4) * mm});
            skLineSegment(sketch, "E96", {"start": v(10.57, -9.4) * mm, "end": v(10, -11.2) * mm});
            skLineSegment(sketch, "E97", {"start": v(18.96, -9.9) * mm, "end": v(18.68, -11.54) * mm});
            skLineSegment(sketch, "E98", {"start": v(18.46, -12.83) * mm, "end": v(18.68, -11.54) * mm});
            skSolve(sketch);
        }
        {
            var Q1;
            Q1=makeQuery(id+"F26.opLoft","CAP_FACE",FACE,{"disambiguationData":[OSD([makeQuery(id+"F25.imprint","IMPRINT",FACE,{"disambiguationData":[TD([[makeQuery(id+"F25.imprint","IMPRINT",EDGE,{"derivedFrom":sQuery(id+"F25.wireOp",EDGE,"E88.0.2")}),1.0]])]})])],"isStart":true});
            var Q2;
            Q2=makeQuery(id+"F29.imprint","IMPRINT",FACE,{"disambiguationData":[TD([[makeQuery(id+"F29.imprint","IMPRINT",EDGE,{"derivedFrom":sQuery(id+"F29.wireOp",EDGE,"E92.0.0")}),1.0]])]});
            loft(context, id + "F30", {"operationType" : NewBodyOperationType.ADD, "sheetProfilesArray" : [{ "sheetProfileEntities" : qUnion([Q1]) }, { "sheetProfileEntities" : qUnion([Q2]) }]});
        }
    });
